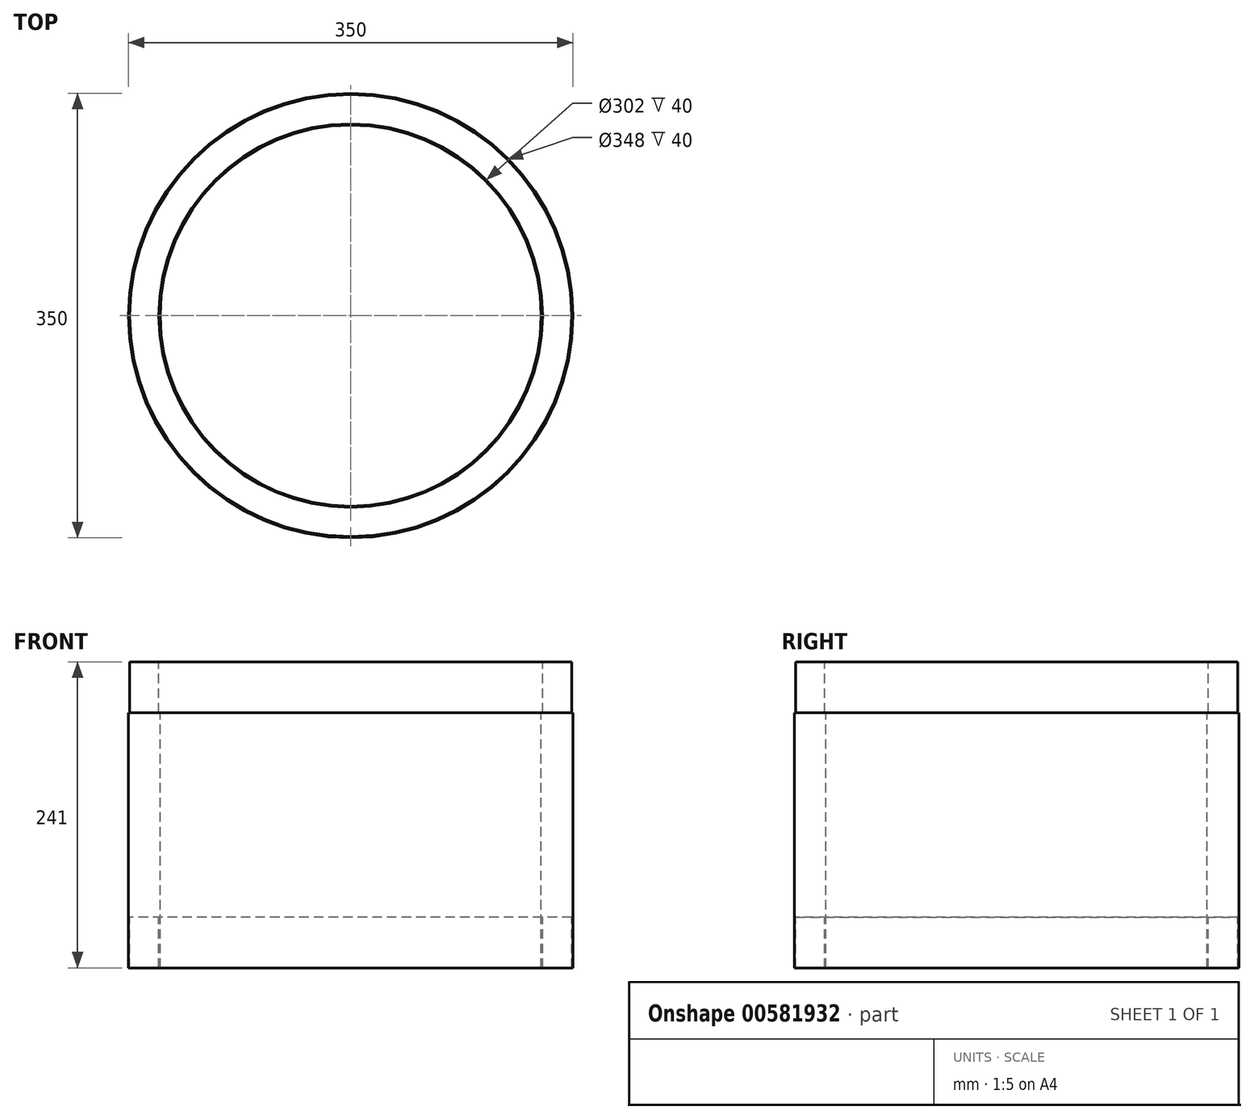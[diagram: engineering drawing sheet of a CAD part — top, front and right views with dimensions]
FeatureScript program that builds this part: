
annotation { "Feature Type Name" : "Feature", "Feature Type Description" : "" }
export const myFeature = defineFeature(function(context is Context, id is Id, definition is map)
    precondition{}
    {
        {
            var Q0;
            Q0=qCreatedBy(makeId("Front.planeOp"),FACE);
            var sketch = newSketch(context, id + "F0", { "sketchPlane" : qUnion([Q0])});
            skLineSegment(sketch, "E0", {"start": v(0, 345.75) * mm, "end": v(0, -558.03) * mm, "construction": true});
            skLineSegment(sketch, "E1", {"start": v(-150, -518.84) * mm, "end": v(-150, -317.84) * mm});
            skLineSegment(sketch, "E2", {"start": v(-150, -317.84) * mm, "end": v(-151, -317.84) * mm});
            skLineSegment(sketch, "E3", {"start": v(-151, -317.84) * mm, "end": v(-151, -277.84) * mm});
            skLineSegment(sketch, "E4", {"start": v(-151, -277.84) * mm, "end": v(-174, -277.84) * mm});
            skLineSegment(sketch, "E5", {"start": v(-174, -277.84) * mm, "end": v(-174, -317.84) * mm});
            skLineSegment(sketch, "E6", {"start": v(-174, -317.84) * mm, "end": v(-175, -317.84) * mm});
            skLineSegment(sketch, "E7", {"start": v(-175, -317.84) * mm, "end": v(-175, -518.84) * mm});
            skLineSegment(sketch, "E8", {"start": v(-175, -518.84) * mm, "end": v(-174, -518.84) * mm});
            skLineSegment(sketch, "E9", {"start": v(-174, -518.84) * mm, "end": v(-174, -478.84) * mm});
            skLineSegment(sketch, "E10", {"start": v(-174, -478.84) * mm, "end": v(-151, -478.84) * mm});
            skLineSegment(sketch, "E11", {"start": v(-151, -478.84) * mm, "end": v(-151, -518.84) * mm});
            skLineSegment(sketch, "E12", {"start": v(-151, -518.84) * mm, "end": v(-150, -518.84) * mm});
            skSolve(sketch);
        }
        {
            var Q0;
            Q0=qSketchRegion(id+"F0",true);
            var Q1;
            Q1=sQuery(id+"F0.wireOp",EDGE,"E0");
            revolve(context, id + "F1", {"entities" : qUnion([Q0]), "axis" : qUnion([Q1]), "revolveType" : RevolveType.FULL});
        }
    });
